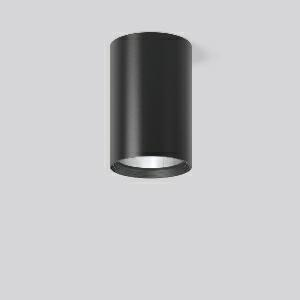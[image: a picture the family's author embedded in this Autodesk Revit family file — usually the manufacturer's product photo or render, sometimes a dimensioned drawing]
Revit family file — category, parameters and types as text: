
# Revit family: heledon_maxi_a_931219_003_738e
name_source: partatom
category: Lighting Fixtures
units: mm (PartAtom-declared; Revit-internal decimal feet)

## family parameters
Cut with Voids When Loaded = No
Host = Face
Light Source = No
Part Type = Normal
Room Calculation Point = No
Round Connector Dimension = Use Diameter
Shared = No

## types (1)
- HELEDON maxi A (1 x LED Modul 930, 3250 lm, 3000)
    Apparent Load = 25 VA
    Approval mark = CE
    CIE Flux Codes = 97 100 100 100 100
    Color Rendering = 90
    Color Temperature = 3000
    Default Elevation = 1800 mm
    Description = Series: HELEDON maxi
Cylindrical surface-mounted downlight. Housing: die-cast aluminium, powder-coated. Internal ceiling frame polycarbonate with bayonet mounting. Black plastic ring and recessed LED to prevent glare from the side. Optical assembly with reflector made of MIRO-Silver with 98% total light reflection for outstanding efficiency - can be changed without tools. Best colour rendering index Ra>90. Suitable for Ceiling mounting. Easy installation with a separate ceiling frame with bayonet mounting and plug connection. Driver integrated. Connected via plug-in connector. High quality converter without flickering and stroboscopic effect. The following accessories can be mounted without use of tools: interchangeable lenses, decorative glasses, honeycomb louvre, clear and frosted diffusers, white interchangeable plastic ring. 
Colour: deep black, matt (RAL 9005)
Diameter: 123 mm
Height: 183 mm
Lamp: LED
Socket: without socket
Colour temperature: 3000K
Colour rendering index (CRI): 92
System power: 25 W
Rated luminous flux: 3250 lm
Luminous efficiency: 130 lm/W
Control gear: Regulated power supply
Protection class: I
Type of protection: IP 20
    Height = 183 mm
    Lamp = 1 x LED Modul 930
    Lamp Light Flux = 3250 lm
    Lamp count = 1
    Length = 123 mm
    Lifetime = 50000 h
    Luminous efficacy = 130 lm/W
    Manufacturer = RZB
    ModVariant = No
    Model = 931219.003
    Mounting Place = Ceiling
    Mounting Type = Surface mounted
    Number of Poles = 1
    OnlyDefault = Yes
    Power Factor = 1
    Product Name = HELEDON maxi A
    Product group = Surface mounted downlights
    ProductGroupID = 302
    Protection Class = Protection class I
    Protection Degree = IP 20
    RLX_Detail_Level = 1
    RLX_Emergency_Light_Flux = 0 lm
    RLX_Emergency_Type = 0
    RLX_Emergency_Type_DB = No
    RlxData = <blob elided: 97065 chars, md5=375acd7c>
    Socket = socket
    Standby Power = 0 W
    System Light Flux = 3250 lm
    System Power = 25 W
    Type Comments = Product without accessories
    Type Image = 931192.003.jpg
    URL = http://relux.com
    VarID = ---
    Voltage = 230 V
    Voltage Range = 220-240 V
    Weight = 0.00 kg
    Width = 0 mm  [stored 0 ft]

note: [stored X ft] marks values corroborated as IEEE doubles in the binary element streams (Revit-internal decimal feet)

## geometry (parser evidence)
native form markers: Blend x4, Sweep x10
no freeform markers — native parametric forms only
